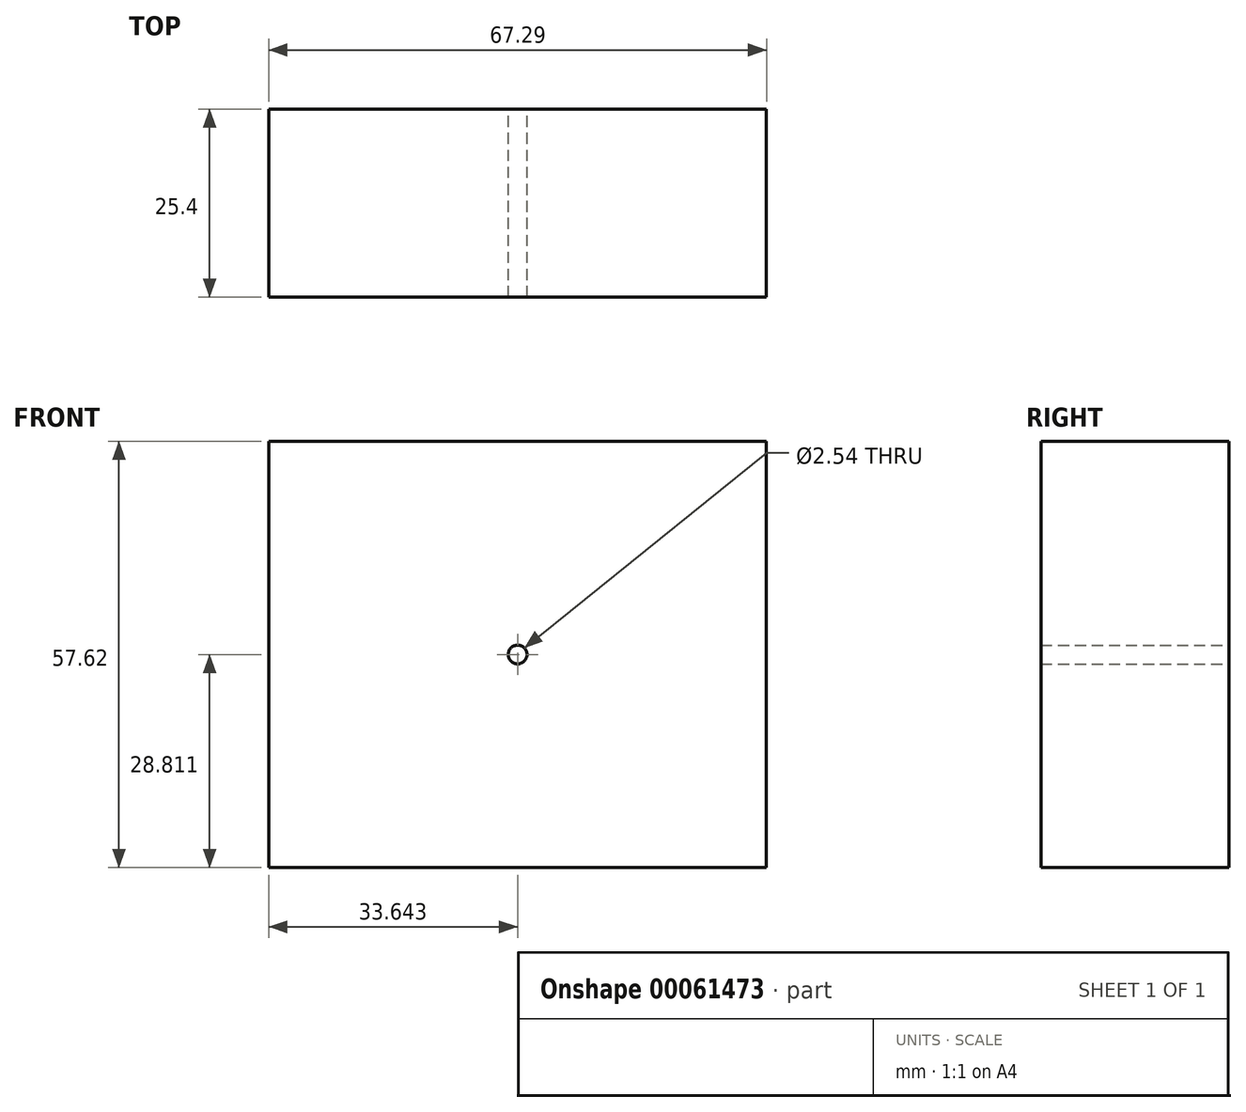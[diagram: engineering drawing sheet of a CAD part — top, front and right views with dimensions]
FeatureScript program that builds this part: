
annotation { "Feature Type Name" : "Feature", "Feature Type Description" : "" }
export const myFeature = defineFeature(function(context is Context, id is Id, definition is map)
    precondition{}
    {
        {
            var Q0;
            Q0=qCreatedBy(makeId("Front.planeOp"),FACE);
            var sketch = newSketch(context, id + "F0", { "sketchPlane" : qUnion([Q0])});
            skLineSegment(sketch, "E0.bottom", {"start": v(0, 0) * mm, "end": v(67.29, 0) * mm});
            skLineSegment(sketch, "E0.top", {"start": v(0, -57.62) * mm, "end": v(67.29, -57.62) * mm});
            skLineSegment(sketch, "E0.left", {"start": v(0, 0) * mm, "end": v(0, -57.62) * mm});
            skLineSegment(sketch, "E0.right", {"start": v(67.29, 0) * mm, "end": v(67.29, -57.62) * mm});
            skSolve(sketch);
        }
        {
            var Q0;
            Q0=makeQuery(id+"F0.imprint","IMPRINT",FACE,{"disambiguationData":[TD([[makeQuery(id+"F0.imprint","IMPRINT",EDGE,{"derivedFrom":sQuery(id+"F0.wireOp",EDGE,"E0.bottom")}),-1.0]])]});
            extrude(context, id + "F1", {"entities" : qUnion([Q0]), "depth" : 25.4 * mm});
        }
        {
            var Q0;
            Q0=makeQuery(id+"F1.opExtrude","CAP_FACE",FACE,{"disambiguationData":[OSD([sQuery(id+"F0.wireOp",EDGE,"E0.bottom"),sQuery(id+"F0.wireOp",EDGE,"E0.top"),sQuery(id+"F0.wireOp",EDGE,"E0.left"),sQuery(id+"F0.wireOp",EDGE,"E0.right")])],"isStart":true});
            var sketch = newSketch(context, id + "F2", { "sketchPlane" : qUnion([Q0])});
            skLineSegment(sketch, "E1", {"start": v(-67.29, -28.8) * mm, "end": v(0, -28.8) * mm});
            skPoint(sketch, "E2", {"position": v(-33.64, -28.8) * mm});
            skSolve(sketch);
        }
        {
            var Q0;
            Q0=sQuery(id+"F2.wireOp",VERTEX,"E2");
            var Q1;
            Q1=makeQuery(id+"F1.opExtrude","SWEPT_BODY",BODY,{"disambiguationData":[OSD([sQuery(id+"F0.wireOp",EDGE,"E0.bottom"),sQuery(id+"F0.wireOp",EDGE,"E0.top"),sQuery(id+"F0.wireOp",EDGE,"E0.left"),sQuery(id+"F0.wireOp",EDGE,"E0.right")])]});
            hole(context, id + "F3", {"style" : HoleStyle.SIMPLE, "holeDiameter" : 2.54 * mm, "endStyle" : HoleEndStyle.THROUGH, "locations" : qUnion([Q0]), "scope" : qUnion([Q1])});
        }
    });
